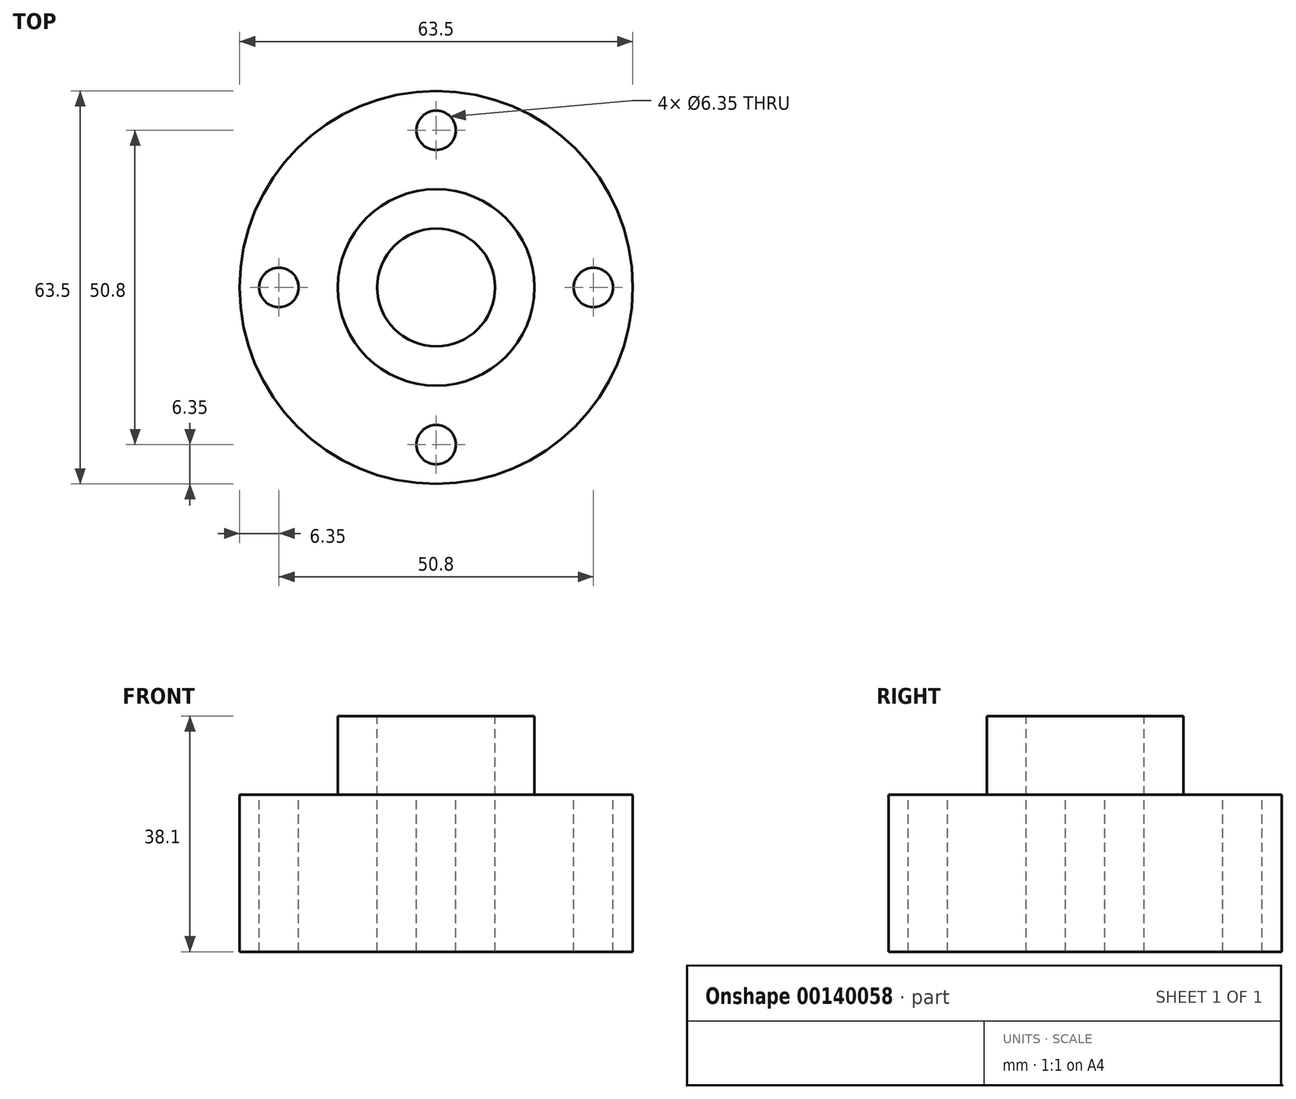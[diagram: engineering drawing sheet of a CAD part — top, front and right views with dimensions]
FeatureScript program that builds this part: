
annotation { "Feature Type Name" : "Feature", "Feature Type Description" : "" }
export const myFeature = defineFeature(function(context is Context, id is Id, definition is map)
    precondition{}
    {
        {
            var Q0;
            Q0=qCreatedBy(makeId("Top.planeOp"),FACE);
            var sketch = newSketch(context, id + "F0", { "sketchPlane" : qUnion([Q0])});
            skCircle(sketch, "E0", {"center": v(0, 0) * mm, "radius": 31.75 * mm});
            skSolve(sketch);
        }
        {
            var Q0;
            Q0 = qSketchRegion(id + "F0", true);
            extrude(context, id + "F1", {"entities" : qUnion([Q0]), "depth" : 25.4 * mm});
        }
        {
            var Q0;
            Q0=makeQuery(id+"F1.opExtrude","CAP_FACE",FACE,{"disambiguationData":[OSD([sQuery(id+"F0.wireOp",EDGE,"E0")])],"isStart":false});
            var sketch = newSketch(context, id + "F2", { "sketchPlane" : qUnion([Q0])});
            skCircle(sketch, "E1", {"center": v(0, 0) * mm, "radius": 15.88 * mm});
            skSolve(sketch);
        }
        {
            var Q0;
            Q0 = qSketchRegion(id + "F2", true);
            extrude(context, id + "F3", {"entities" : qUnion([Q0]), "operationType" : NewBodyOperationType.ADD, "depth" : 12.7 * mm});
        }
        {
            var Q0;
            Q0=makeQuery(id+"F3.opExtrude","CAP_FACE",FACE,{"disambiguationData":[OSD([sQuery(id+"F2.wireOp",EDGE,"E1")])],"isStart":false});
            var sketch = newSketch(context, id + "F4", { "sketchPlane" : qUnion([Q0])});
            skCircle(sketch, "E2", {"center": v(0, 0) * mm, "radius": 9.53 * mm});
            skSolve(sketch);
        }
        {
            var Q0;
            Q0 = qSketchRegion(id + "F4", true);
            extrude(context, id + "F5", {"entities" : qUnion([Q0]), "operationType" : NewBodyOperationType.REMOVE, "endBound" : BoundingType.THROUGH_ALL, "oppositeDirection" : true, "depth" : 25.4 * mm});
        }
        {
            var Q0;
            Q0=makeQuery(id+"F1.opExtrude","CAP_FACE",FACE,{"disambiguationData":[OSD([sQuery(id+"F0.wireOp",EDGE,"E0")])],"isStart":false});
            var sketch = newSketch(context, id + "F6", { "sketchPlane" : qUnion([Q0])});
            skCircle(sketch, "E3", {"center": v(0, 0) * mm, "radius": 25.4 * mm, "construction": true});
            skCircle(sketch, "E4", {"center": v(0, 25.4) * mm, "radius": 3.18 * mm});
            skCircle(sketch, "E5", {"center": v(-25.4, 0) * mm, "radius": 3.18 * mm});
            skCircle(sketch, "E6", {"center": v(0, -25.4) * mm, "radius": 3.18 * mm});
            skCircle(sketch, "E7", {"center": v(25.4, 0) * mm, "radius": 3.18 * mm});
            skSolve(sketch);
        }
        {
            var Q0;
            Q0 = qSketchRegion(id + "F6", true);
            extrude(context, id + "F7", {"entities" : qUnion([Q0]), "operationType" : NewBodyOperationType.REMOVE, "endBound" : BoundingType.THROUGH_ALL, "oppositeDirection" : true, "depth" : 25.4 * mm});
        }
    });
